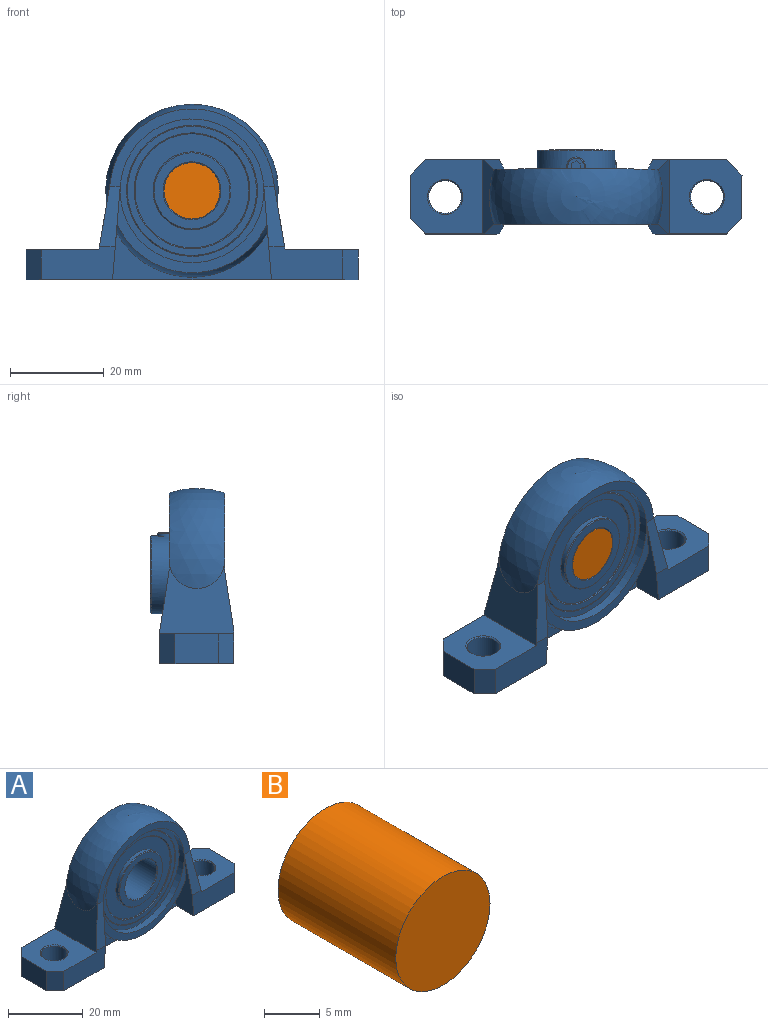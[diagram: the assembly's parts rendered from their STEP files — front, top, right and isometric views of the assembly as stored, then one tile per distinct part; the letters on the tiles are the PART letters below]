
ASSEMBLY  parts=2 mates=1
PART A: 87 faces, bbox 71.7x37.7x38.2 mm
  f0: plane 34x10.09mm, normal (0,-1,0), area 115.1mm2, adj f2,f4,f6,f62
  f1: plane 34x10.09mm, normal (0,1,0), area 115.1mm2, adj f3,f5,f7,f62
  f2: plane 20.7x7.37mm, normal (-1,0,-0.08), area 77.6mm2, adj f0,f4,f54,f57,f58,f62
  f3: plane 20.7x7.37mm, normal (-1,0,-0.08), area 77.6mm2, adj f1,f5,f52,f59,f60,f62
  f4: sphere r=18.5mm, area 192.3mm2, adj f0,f2,f6,f58
  f5: sphere r=18.5mm, area 192.3mm2, adj f1,f3,f7,f52
  f6: plane 20.7x7.37mm, normal (1,0,-0.08), area 77.6mm2, adj f0,f4,f49,f51,f58,f62
  f7: plane 20.7x7.37mm, normal (1,0,-0.08), area 77.6mm2, adj f1,f5,f48,f50,f52,f62
  f8: cone r=1.75mm half-angle=45deg, axis (-0.87,0,0.5), area 4.2mm2, adj f9,f10
  f9: cylinder r=2mm len=4mm, axis (0.87,0,-0.5), area 8.5mm2, adj f8,f76
  f10: plane 3.5x3.03mm, normal (0.87,0,-0.5), area 6.2mm2, adj f8,f11,f12,f13,f14,f15,f16
  f11: plane 2.25x1.89mm, normal (0.22,0.89,0.39), area 2.3mm2, adj f10,f12,f16,f17
  f12: plane 1.77x1.15mm, normal (0.5,0.06,0.86), area 2.3mm2, adj f10,f11,f13,f17
  f13: plane 2.21x1.83mm, normal (0.28,-0.83,0.48), area 2.3mm2, adj f10,f12,f14,f17
  f14: plane 2.25x1.89mm, normal (-0.22,-0.89,-0.39), area 2.3mm2, adj f10,f13,f15,f17
  f15: plane 1.77x1.15mm, normal (-0.5,-0.06,-0.86), area 2.3mm2, adj f10,f14,f16,f17
  f16: plane 2.21x1.83mm, normal (-0.28,0.83,-0.48), area 2.3mm2, adj f10,f11,f15,f17
  f17: plane 2.3x1.79mm, normal (0.87,0,-0.5), area 3.5mm2, adj f11,f12,f13,f14,f15,f16
  f18: cylinder r=2mm len=4mm, axis (0.87,0,-0.5), area 10.4mm2, adj f19,f78
  f19: plane 4x3.46mm, normal (-0.87,0,0.5), area 12.6mm2, adj f18
  f20: cone r=1.75mm half-angle=45deg, axis (0,0,-1), area 4.2mm2, adj f21,f22
  f21: cylinder r=2mm len=4mm, axis (0,0,1), area 8.5mm2, adj f20,f76
  f22: plane 3.5x3.5mm, normal (0,0,1), area 6.2mm2, adj f20,f23,f24,f25,f26,f27,f28
  f23: plane 2x1.03mm, normal (-0.45,0.89,0), area 2.3mm2, adj f22,f24,f28,f29
  f24: plane 2x1.15mm, normal (-1,0.06,0), area 2.3mm2, adj f22,f23,f25,f29
  f25: plane 2x0.96mm, normal (-0.55,-0.83,0), area 2.3mm2, adj f22,f24,f26,f29
  f26: plane 2x1.03mm, normal (0.45,-0.89,0), area 2.3mm2, adj f22,f25,f27,f29
  f27: plane 2x1.15mm, normal (1,-0.06,0), area 2.3mm2, adj f22,f26,f28,f29
  f28: plane 2x0.96mm, normal (0.55,0.83,0), area 2.3mm2, adj f22,f23,f27,f29
  f29: plane 2.3x2.07mm, normal (0,0,1), area 3.5mm2, adj f23,f24,f25,f26,f27,f28
  f30: cylinder r=2mm len=4mm, axis (0,0,1), area 10.4mm2, adj f31,f78
  f31: plane 4x4mm, normal (0,0,-1), area 12.6mm2, adj f30
  f32: sphere r=18.5mm, area 728.3mm2, adj f39,f40,f41,f52,f53,f55,f56,f58
  f33: cylinder r=15.38mm len=30.75mm, axis (0,1,0), area 186mm2, adj f37,f52
  f34: cylinder r=14mm len=28mm, axis (0,1,0), area 17.6mm2, adj f37,f80
  f35: plane 30.75x30.75mm, normal (0,-1,0), area 126.9mm2, adj f36,f38
  f36: cylinder r=15.38mm len=30.75mm, axis (0,1,0), area 186mm2, adj f35,f58
  f37: plane 30.75x30.75mm, normal (0,1,0), area 126.9mm2, adj f33,f34
  f38: cylinder r=14mm len=28mm, axis (0,1,0), area 17.6mm2, adj f35,f82
  f39: plane 15.85x15.51mm, normal (-0.99,0,0.17), area 160.3mm2, adj f32,f40,f41,f43,f48,f49,f50,f51
  f40: plane 0.01x0mm, normal (0.64,0,0.77), area 0mm2, adj f32,f39,f52
  f41: plane 0.01x0mm, normal (0.64,0,0.77), area 0mm2, adj f32,f39,f58
  f42: cone r=3.75mm half-angle=45deg, axis (0,0,1), area 8.1mm2, adj f43,f44
  f43: plane 15.85x15.6mm, normal (0,0,1), area 192.5mm2, adj f39,f42,f45,f46,f47,f50,f51
  f44: cylinder r=3.5mm len=7mm, axis (0,0,1), area 135.2mm2, adj f42,f62
  f45: plane 6.4x3.25mm, normal (-0.71,-0.71,0), area 29.4mm2, adj f43,f46,f51,f62
  f46: plane 9.35x6.4mm, normal (-1,0,0), area 59.8mm2, adj f43,f45,f47,f62
  f47: plane 6.4x3.25mm, normal (-0.71,0.71,0), area 29.4mm2, adj f43,f46,f50,f62
  f48: plane 13x4.45mm, normal (0,0.99,0.15), area 37.1mm2, adj f7,f39,f50,f52
  f49: plane 13x4.45mm, normal (0,-0.99,0.15), area 37.1mm2, adj f6,f39,f51,f58
  f50: plane 15.83x7mm, normal (0,1,0), area 101.3mm2, adj f7,f39,f43,f47,f48,f62
  f51: plane 15.83x7mm, normal (0,-1,0), area 101.3mm2, adj f6,f39,f43,f45,f49,f62
  f52: plane 35.22x35.05mm, normal (0,1,0), area 199.5mm2, adj f3,f5,f7,f32,f33,f39,f40,f48
  f53: plane 0.01x0mm, normal (-0.64,0,0.77), area 0mm2, adj f32,f52,f56
  f54: plane 15.83x7mm, normal (0,-1,0), area 101.3mm2, adj f2,f56,f57,f62,f64,f66
  f55: plane 0.01x0mm, normal (-0.64,0,0.77), area 0mm2, adj f32,f56,f58
  f56: plane 15.85x15.51mm, normal (0.99,0,0.17), area 160.3mm2, adj f32,f52,f53,f54,f55,f57,f58,f59
  f57: plane 13x4.45mm, normal (0,-0.99,0.15), area 37.1mm2, adj f2,f54,f56,f58
  f58: plane 35.22x35.05mm, normal (0,-1,0), area 199.5mm2, adj f2,f4,f6,f32,f36,f39,f41,f49
  f59: plane 13x4.45mm, normal (0,0.99,0.15), area 37.1mm2, adj f3,f52,f56,f60
  f60: plane 15.83x7mm, normal (0,1,0), area 101.3mm2, adj f3,f56,f59,f61,f62,f66
  f61: plane 6.4x3.25mm, normal (0.71,0.71,0), area 29.4mm2, adj f60,f62,f63,f66
  f62: plane 71x15.85mm, normal (0,0,-1), area 573.4mm2, adj f0,f1,f2,f3,f6,f7,f44,f45
  f63: plane 9.35x6.4mm, normal (1,0,0), area 59.8mm2, adj f61,f62,f64,f66
  f64: plane 6.4x3.25mm, normal (0.71,-0.71,0), area 29.4mm2, adj f54,f62,f63,f66
  f65: cylinder r=3.5mm len=7mm, axis (0,0,1), area 135.2mm2, adj f62,f67
  f66: plane 15.85x15.6mm, normal (0,0,1), area 192.5mm2, adj f54,f56,f60,f61,f63,f64,f67
  f67: cone r=3.75mm half-angle=45deg, axis (0,0,1), area 8.1mm2, adj f65,f66
  f68: cone r=8.12mm half-angle=45deg, axis (0,1,0), area 14.6mm2, adj f69,f70
  f69: plane 16.24x16.24mm, normal (0,-1,0), area 86.4mm2, adj f68,f79
  f70: cylinder r=8.32mm len=16.64mm, axis (0,1,0), area 54.9mm2, adj f68,f85
  f71: cone r=12.4mm half-angle=45deg, axis (0,-1,0), area 21.9mm2, adj f72,f73
  f72: plane 27.6x27.6mm, normal (0,-1,0), area 115.2mm2, adj f71,f82
  f73: cylinder r=12.2mm len=24.4mm, axis (0,1,0), area 3.8mm2, adj f71,f85
  f74: cone r=8.12mm half-angle=45deg, axis (0,-1,0), area 14.6mm2, adj f75,f76
  f75: plane 16.24x16.24mm, normal (0,1,0), area 86.4mm2, adj f74,f77
  f76: cylinder r=8.32mm len=16.64mm, axis (0,1,0), area 290.4mm2, adj f9,f21,f74,f86
  f77: cone r=6.2mm half-angle=45deg, axis (0,1,0), area 10.8mm2, adj f75,f78
  f78: cylinder r=6mm len=14.6mm, axis (0,1,0), area 524.6mm2, adj f18,f30,f77,f79
  f79: cone r=6.2mm half-angle=45deg, axis (0,-1,0), area 10.8mm2, adj f69,f78
  f80: cone r=13.8mm half-angle=45deg, axis (0,-1,0), area 24.7mm2, adj f34,f81
  f81: plane 27.6x27.6mm, normal (0,1,0), area 115.2mm2, adj f80,f83
  f82: cone r=13.8mm half-angle=45deg, axis (0,1,0), area 24.7mm2, adj f38,f72
  f83: cone r=12.4mm half-angle=45deg, axis (0,1,0), area 21.9mm2, adj f81,f84
  f84: cylinder r=12.2mm len=24.4mm, axis (0,1,0), area 3.8mm2, adj f83,f86
  f85: plane 24.4x24.4mm, normal (0,-1,0), area 250.1mm2, adj f70,f73
  f86: plane 24.4x24.4mm, normal (0,1,0), area 250.1mm2, adj f76,f84
PART B: 3 faces, bbox 12x15x12 mm
  f0: plane 12x12mm, normal (0,-1,0), area 113.1mm2, adj f2
  f1: plane 12x12mm, normal (0,1,0), area 113.1mm2, adj f2
  f2: cylinder r=6mm len=15mm, axis (0,1,0), area 565.5mm2, adj f0,f1
PLACE A at identity
PLACE B rot(axis=(0,-1,0),7.1deg) t=(0,0,0)mm
MATE revolute A.f74 <-> B.f2  axis (0,-1,0) through (0,-5,0)mm
